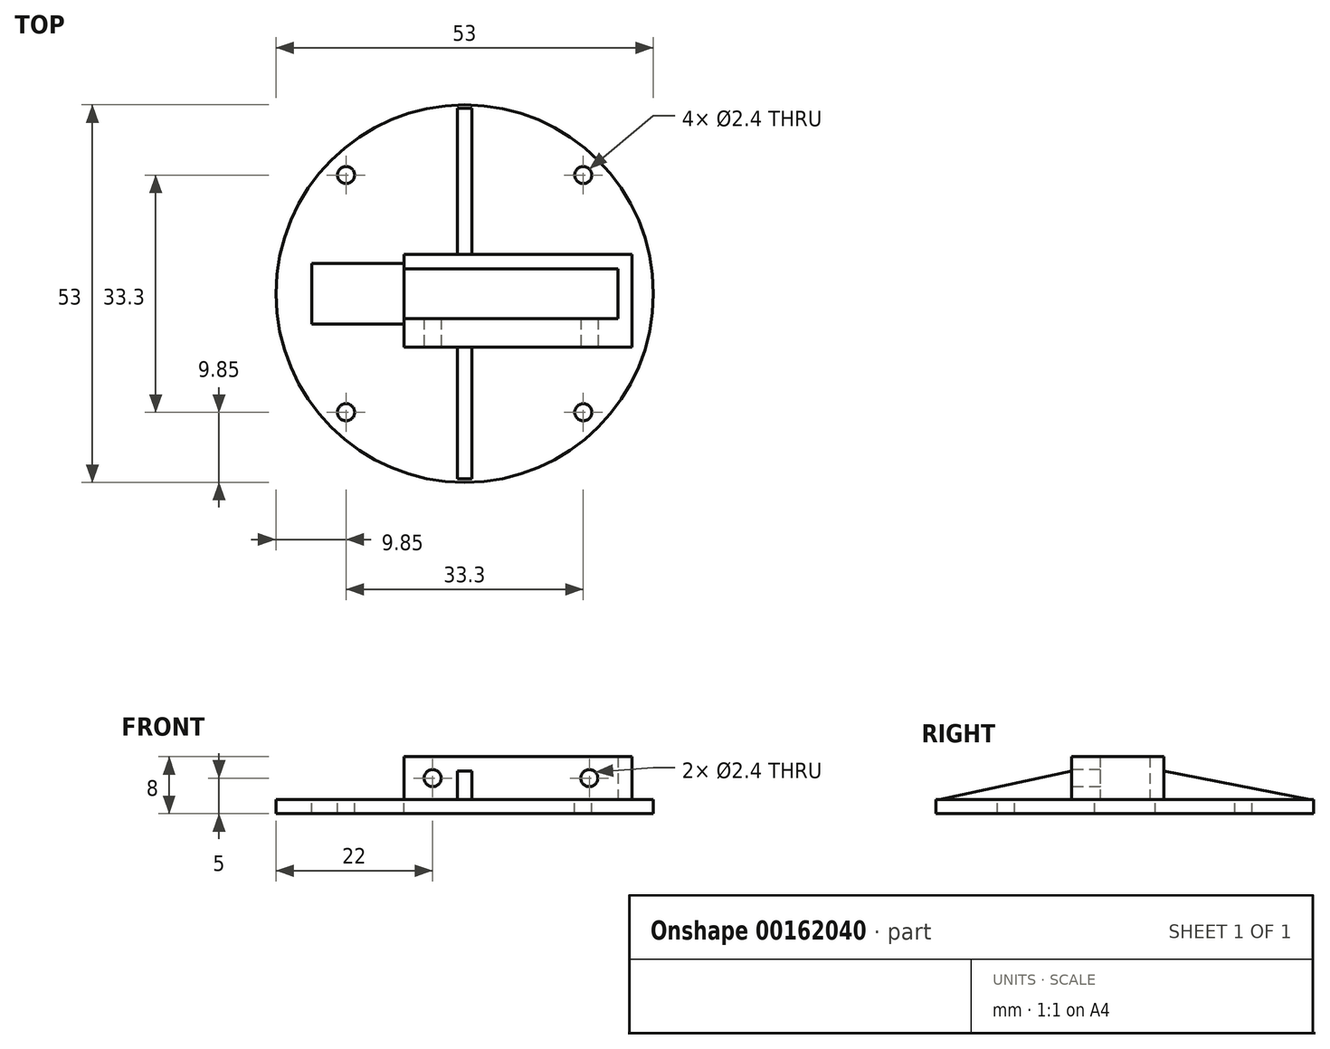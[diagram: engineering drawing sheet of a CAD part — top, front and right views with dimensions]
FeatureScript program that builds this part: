
annotation { "Feature Type Name" : "Feature", "Feature Type Description" : "" }
export const myFeature = defineFeature(function(context is Context, id is Id, definition is map)
    precondition{}
    {
        {
            var Q0;
            Q0=qCreatedBy(makeId("Top.planeOp"),FACE);
            var sketch = newSketch(context, id + "F0", { "sketchPlane" : qUnion([Q0])});
            skCircle(sketch, "E0", {"center": v(0, 0) * mm, "radius": 26.5 * mm});
            skLineSegment(sketch, "E1.bottom", {"start": v(-21.5, 4.25) * mm, "end": v(-8.5, 4.25) * mm});
            skLineSegment(sketch, "E1.top", {"start": v(-21.5, -4.25) * mm, "end": v(-8.5, -4.25) * mm});
            skLineSegment(sketch, "E1.left", {"start": v(-21.5, 4.25) * mm, "end": v(-21.5, -4.25) * mm});
            skLineSegment(sketch, "E1.right", {"start": v(-8.5, 4.25) * mm, "end": v(-8.5, -4.25) * mm});
            skLineSegment(sketch, "E2", {"start": v(26.5, 0) * mm, "end": v(-26.5, 0) * mm, "construction": true});
            skLineSegment(sketch, "E3.bottom", {"start": v(-8.5, 5.5) * mm, "end": v(23.5, 5.5) * mm, "construction": true});
            skLineSegment(sketch, "E3.top", {"start": v(-8.5, -7.5) * mm, "end": v(23.5, -7.5) * mm, "construction": true});
            skLineSegment(sketch, "E3.left", {"start": v(-8.5, 5.5) * mm, "end": v(-8.5, -7.5) * mm, "construction": true});
            skLineSegment(sketch, "E3.right", {"start": v(23.5, 5.5) * mm, "end": v(23.5, -7.5) * mm, "construction": true});
            skCircle(sketch, "E4", {"center": v(-16.65, 16.65) * mm, "radius": 1.2 * mm});
            skCircle(sketch, "E5.MirrorC", {"center": v(16.65, 16.65) * mm, "radius": 1.2 * mm});
            skCircle(sketch, "E6.MirrorC", {"center": v(-16.65, -16.65) * mm, "radius": 1.2 * mm});
            skCircle(sketch, "E7.MirrorC", {"center": v(16.65, -16.65) * mm, "radius": 1.2 * mm});
            skLineSegment(sketch, "E8.bottom", {"start": v(-1.5, 25.5) * mm, "end": v(1.5, 25.5) * mm, "construction": true});
            skLineSegment(sketch, "E8.top", {"start": v(-1.5, -26) * mm, "end": v(1.5, -26) * mm, "construction": true});
            skLineSegment(sketch, "E8.left", {"start": v(-1.5, 25.5) * mm, "end": v(-1.5, -26) * mm, "construction": true});
            skLineSegment(sketch, "E8.right", {"start": v(1.5, 25.5) * mm, "end": v(1.5, -26) * mm, "construction": true});
            skLineSegment(sketch, "E9.0", {"start": v(-8.5, 3.5) * mm, "end": v(21.5, 3.5) * mm, "construction": true});
            skLineSegment(sketch, "E10.0", {"start": v(-8.5, -3.5) * mm, "end": v(21.5, -3.5) * mm, "construction": true});
            skLineSegment(sketch, "E11.0", {"start": v(21.5, 3.5) * mm, "end": v(21.5, -3.5) * mm, "construction": true});
            skSolve(sketch);
        }
        {
            var Q0;
            Q0=qSketchRegion(id+"F0",true);
            extrude(context, id + "F1", {"entities" : qUnion([Q0]), "oppositeDirection" : true, "depth" : 2 * mm});
        }
        {
            var Q0;
            Q0=makeQuery(id+"F1.opExtrude","CAP_FACE",FACE,{"disambiguationData":[OSD([sQuery(id+"F0.wireOp",EDGE,"E0"),sQuery(id+"F0.wireOp",EDGE,"E1.bottom"),sQuery(id+"F0.wireOp",EDGE,"E1.top"),sQuery(id+"F0.wireOp",EDGE,"E1.left"),sQuery(id+"F0.wireOp",EDGE,"E1.right"),sQuery(id+"F0.wireOp",EDGE,"E4"),sQuery(id+"F0.wireOp",EDGE,"E5.MirrorC"),sQuery(id+"F0.wireOp",EDGE,"E6.MirrorC"),sQuery(id+"F0.wireOp",EDGE,"E7.MirrorC")])],"isStart":true});
            var sketch = newSketch(context, id + "F2", { "sketchPlane" : qUnion([Q0])});
            skLineSegment(sketch, "E12.0", {"start": v(-8.5, 5.5) * mm, "end": v(23.5, 5.5) * mm});
            skLineSegment(sketch, "E13.0", {"start": v(-8.5, 3.5) * mm, "end": v(21.5, 3.5) * mm});
            skLineSegment(sketch, "E14.0", {"start": v(23.5, 5.5) * mm, "end": v(23.5, -7.5) * mm});
            skLineSegment(sketch, "E15.0", {"start": v(-8.5, -7.5) * mm, "end": v(23.5, -7.5) * mm});
            skLineSegment(sketch, "E16.0", {"start": v(-8.5, -3.5) * mm, "end": v(21.5, -3.5) * mm});
            skLineSegment(sketch, "E17.0", {"start": v(-8.5, 5.5) * mm, "end": v(-8.5, 3.5) * mm});
            skLineSegment(sketch, "E18.trimOffspring", {"start": v(-8.5, -3.5) * mm, "end": v(-8.5, -7.5) * mm});
            skLineSegment(sketch, "E19.0", {"start": v(21.5, 3.5) * mm, "end": v(21.5, -3.5) * mm});
            skSolve(sketch);
        }
        {
            var Q0;
            Q0=qSketchRegion(id+"F2",true);
            extrude(context, id + "F3", {"entities" : qUnion([Q0]), "operationType" : NewBodyOperationType.ADD, "depth" : 6 * mm});
        }
        {
            var Q0;
            Q0=qCreatedBy(makeId("Right.planeOp"),FACE);
            var sketch = newSketch(context, id + "F4", { "sketchPlane" : qUnion([Q0])});
            skLineSegment(sketch, "E20", {"start": v(-7.5, 0) * mm, "end": v(-7.5, 4) * mm});
            skLineSegment(sketch, "E21", {"start": v(-7.5, 4) * mm, "end": v(-26, 0) * mm});
            skLineSegment(sketch, "E22", {"start": v(-26, 0) * mm, "end": v(-7.5, 0) * mm});
            skLineSegment(sketch, "E23.MirrorCS", {"start": v(5.5, 0) * mm, "end": v(5.5, 4) * mm});
            skLineSegment(sketch, "E24.MirrorCS", {"start": v(5.5, 4) * mm, "end": v(26, 0) * mm});
            skLineSegment(sketch, "E25.MirrorCS", {"start": v(26, 0) * mm, "end": v(5.5, 0) * mm});
            skSolve(sketch);
        }
        {
            var Q0;
            Q0=qSketchRegion(id+"F4",true);
            extrude(context, id + "F5", {"entities" : qUnion([Q0]), "operationType" : NewBodyOperationType.ADD, "depth" : 2 * mm, "symmetric" : true});
        }
        {
            var Q0;
            Q0=makeQuery(id+"F3.opExtrude","SWEPT_FACE",FACE,{"disambiguationData":[OSD([sQuery(id+"F2.wireOp",EDGE,"E15.0")])]});
            var sketch = newSketch(context, id + "F6", { "sketchPlane" : qUnion([Q0])});
            skCircle(sketch, "E26", {"center": v(-4.5, 3) * mm, "radius": 1.2 * mm});
            skCircle(sketch, "E27", {"center": v(17.5, 3) * mm, "radius": 1.2 * mm});
            skSolve(sketch);
        }
        {
            var Q0;
            Q0=qSketchRegion(id+"F6",true);
            extrude(context, id + "F7", {"entities" : qUnion([Q0]), "operationType" : NewBodyOperationType.REMOVE, "endBound" : BoundingType.UP_TO_NEXT, "oppositeDirection" : true, "depth" : 25 * mm});
        }
    });
